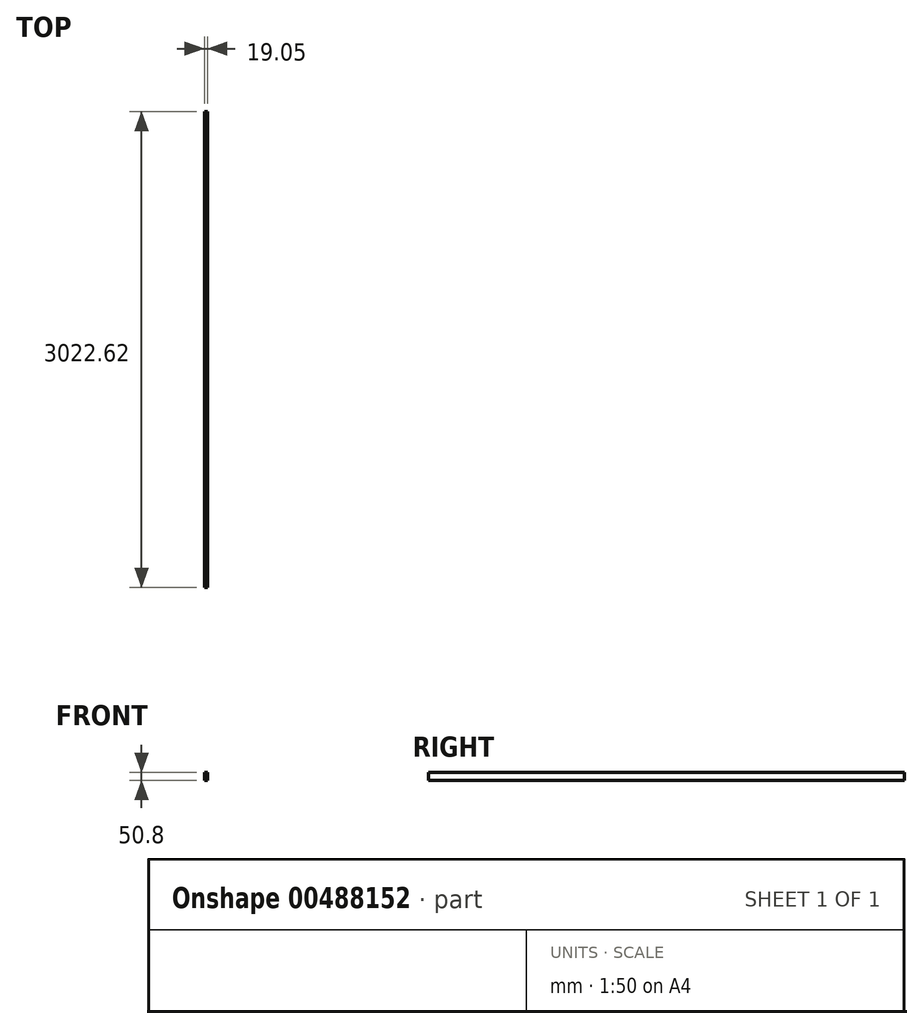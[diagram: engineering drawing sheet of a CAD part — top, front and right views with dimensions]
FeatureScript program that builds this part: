
annotation { "Feature Type Name" : "Feature", "Feature Type Description" : "" }
export const myFeature = defineFeature(function(context is Context, id is Id, definition is map)
    precondition{}
    {
        {
            var Q0;
            Q0=qCreatedBy(makeId("Front.planeOp"),FACE);
            var sketch = newSketch(context, id + "F0", { "sketchPlane" : qUnion([Q0])});
            skLineSegment(sketch, "E0", {"start": v(0, 0) * mm, "end": v(19.05, 0) * mm});
            skLineSegment(sketch, "E1", {"start": v(0, 0) * mm, "end": v(0, -50.8) * mm});
            skLineSegment(sketch, "E2", {"start": v(0, -50.8) * mm, "end": v(19.05, -50.8) * mm});
            skLineSegment(sketch, "E3", {"start": v(19.05, -50.8) * mm, "end": v(19.05, 0) * mm});
            skSolve(sketch);
        }
        {
            var Q0;
            Q0=makeQuery(id+"F0.imprint","IMPRINT",FACE,{"disambiguationData":[TD([[makeQuery(id+"F0.imprint","IMPRINT",EDGE,{"derivedFrom":sQuery(id+"F0.wireOp",EDGE,"E0")}),-1.0]])]});
            extrude(context, id + "F1", {"entities" : qUnion([Q0]), "oppositeDirection" : true, "depth" : 2743.2 * mm + 279.4 * mm + 5 / 203.2 * mm, "offsetDistance" : 25.4 * mm});
        }
    });
